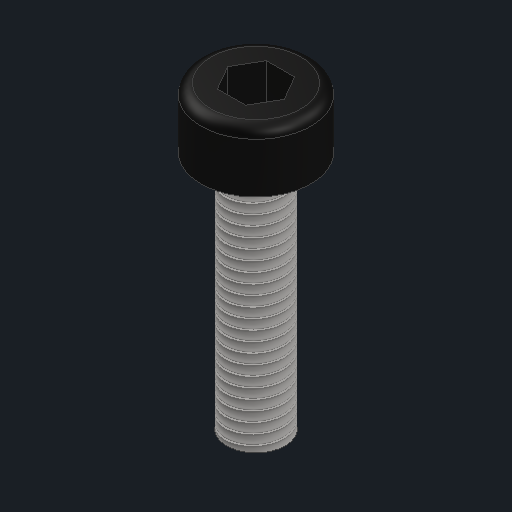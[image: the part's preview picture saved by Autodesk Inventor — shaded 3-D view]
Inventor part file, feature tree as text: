
AUTODESK INVENTOR PART (.ipt)
format: ipt  version: 2025.1 (Build 291241000, 241)  size: 151,040 bytes
history: native  units: mm
features: other x3, sketch x1
ambient origin geometry x8: Origin, YZ Plane, XZ Plane, XY Plane, X Axis, Y Axis, Z Axis, Center Point
bodies: Solid1 (feature_tree)
feature tree (4):
  other  "M3x12.ipt"
  other  "Solid1::M3x12.ipt"
  other  "TaggingFeature1"
  sketch  "Sketch1"  dims[d0=10.0mm]
